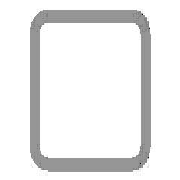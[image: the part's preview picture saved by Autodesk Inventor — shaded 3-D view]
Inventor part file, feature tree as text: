
AUTODESK INVENTOR PART (.ipt)
format: ipt  version: 2025 (Build 290162010, 162A)  size: 135,680 bytes
history: native  units: mm (DEFAULTED — no unit token found)
features: other x4, sketch x1, plane x1
ambient origin geometry x8: Origin, YZ Plane, XZ Plane, XY Plane, X Axis, Y Axis, Z Axis, Center Point
bodies: Solid1 (feature_tree), Body (feature_tree)
feature tree (6):
  parser-record x1  (decoder bookkeeping rows leaked as tree rows — omitted from the tree; the rows remain in map.json)
  other  "Driven Length"
  other  "Start Plane"
  other  "End Plane"
  sketch  "Sketch3"  dims[d3=1500.0mm d4=0.0mm d7=8.0mm d9=60.0mm d11=60.0mm d12=4.0mm d13=-0.0mm d14=1500.0mm d15=30.0mm d16=30.0mm d17=90.0deg d18=1500.0mm]
  plane  "Work Plane3"
